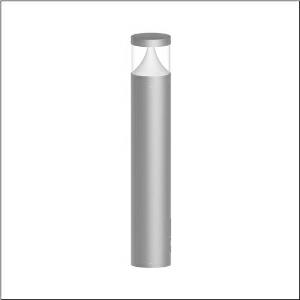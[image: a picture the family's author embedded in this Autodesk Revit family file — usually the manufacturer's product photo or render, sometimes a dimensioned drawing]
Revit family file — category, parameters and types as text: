
# Revit family: cl_31_poller_90_5cl444603
name_source: partatom
category: Lighting Fixtures
units: mm (PartAtom-declared; Revit-internal decimal feet)

## family parameters
Cut with Voids When Loaded = No
Host = Face
Light Source = No
Part Type = Normal
Room Calculation Point = No
Round Connector Dimension = Use Diameter
Shared = No

## types (1)
- --- (1 x LED, 1500 lm, 14 W, 3000K)
    Apparent Load = 14 VA
    CIE Flux Codes = 19 66 88 92 100
    Color Rendering = 80
    Color Temperature = 3000K
    Default Elevation = 1800 mm
    Description = CL 31 Bollard 90, bollard luminaire, primary light control with lens, of PC, primary optical cover: cover panel, of PC, transparent, secondary light control with reflector, of PC, primary light characteristic: asymmetric, LED, rated luminous flux: 1.500lm, luminous efficacy: 107lm/W, light colour: 830, colour temperature: 3000K, control gear: DALI, with terminal, 5-pole, max. 2.5mm², mains connection: 220..240V, AC, 50/60Hz, rated input power: 14W, luminaire housing, of aluminium, powder-coated, SITECO metallic grey, diameter: 170mm, height: 900mm, protection rating (complete): IP65, insulation class (complete): insulation class I (protective earthing), certification: CE, ENEC, impact resistance: IK10, permissible operating ambient temperature for outdoor applications: -20..+50°C, packaging unit: 1 piece
    Height = 200 mm  [stored 0.656168 ft]
    Lamp = 1 x LED
    Lamp Light Flux = 1500 lm
    Lamp Power = 14 W
    Lamp count = 1
    Length = 170 mm  [stored 0.557743 ft]
    Luminous efficacy = 107 lm/W
    Manufacturer = Siteco
    ModVariant = No
    Model = 5CL444603
    Mounting Place = Floor
    Mounting Type = Freestanding
    Number of Poles = 1
    OnlyDefault = Yes
    Power Factor = 1
    Product Name = CL 31 Poller 90
    Product group = bollard luminaire
    ProductGroupID = 1304
    Protection Class = Protection class I
    Protection Degree = IP 65
    RLX_Detail_Level = 1
    RLX_Emergency_Light_Flux = 0 lm
    RLX_Emergency_Type = 0
    RLX_Emergency_Type_DB = No
    RlxData = <blob elided: 64897 chars, md5=c3178e56>
    Socket = socket
    Standby Power = 0 W
    System Light Flux = 1500 lm
    System Power = 14 W
    Type Comments = factory setting: luminous flux: 100 % | dim-lin: 254 | 350 mA
    Type Image = l_1006899.jpg
    URL = http://relux.com
    VarID = @adj_192701
    Voltage = 0 V
    Weight = 0.00 kg
    Width = 0 mm  [stored 0 ft]

note: [stored X ft] marks values corroborated as IEEE doubles in the binary element streams (Revit-internal decimal feet)

## geometry (parser evidence)
native form markers: Blend x4, Sweep x11
no freeform markers — native parametric forms only
